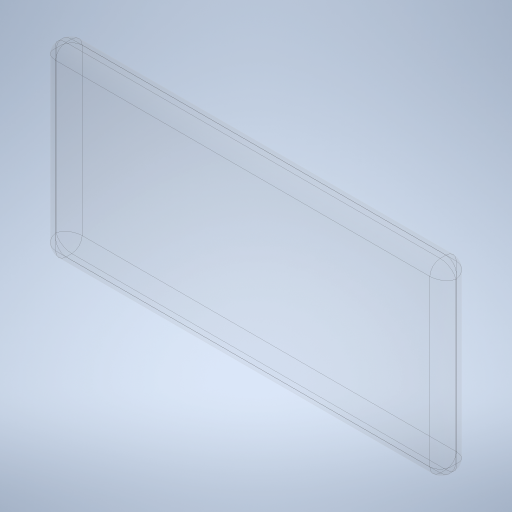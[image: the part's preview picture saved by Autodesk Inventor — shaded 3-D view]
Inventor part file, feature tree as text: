
AUTODESK INVENTOR PART (.ipt)
format: ipt  version: 2023 (Build 270158030, 158C)  size: 311,296 bytes
history: native  units: mm
features: fillet x2, other x1, extrude x1, sketch x1
ambient origin geometry x8: Origin, YZ Plane, XZ Plane, XY Plane, X Axis, Y Axis, Z Axis, Center Point
bodies: Body1 (feature_tree)
feature tree (5):
  other  "samsung-s20"
  extrude  "Extrusion1"  Depth=35.75mm
  fillet  "Fillet1"  Radius=154.0mm
  fillet  "Fillet2"  Radius=77.0mm
  sketch  "Sketch1"  dims[d0=71.5mm d1=35.75mm d2=154.0mm d3=77.0mm d4=10.2mm d5=0.0mm d6=4.0mm d7=5.0mm]
